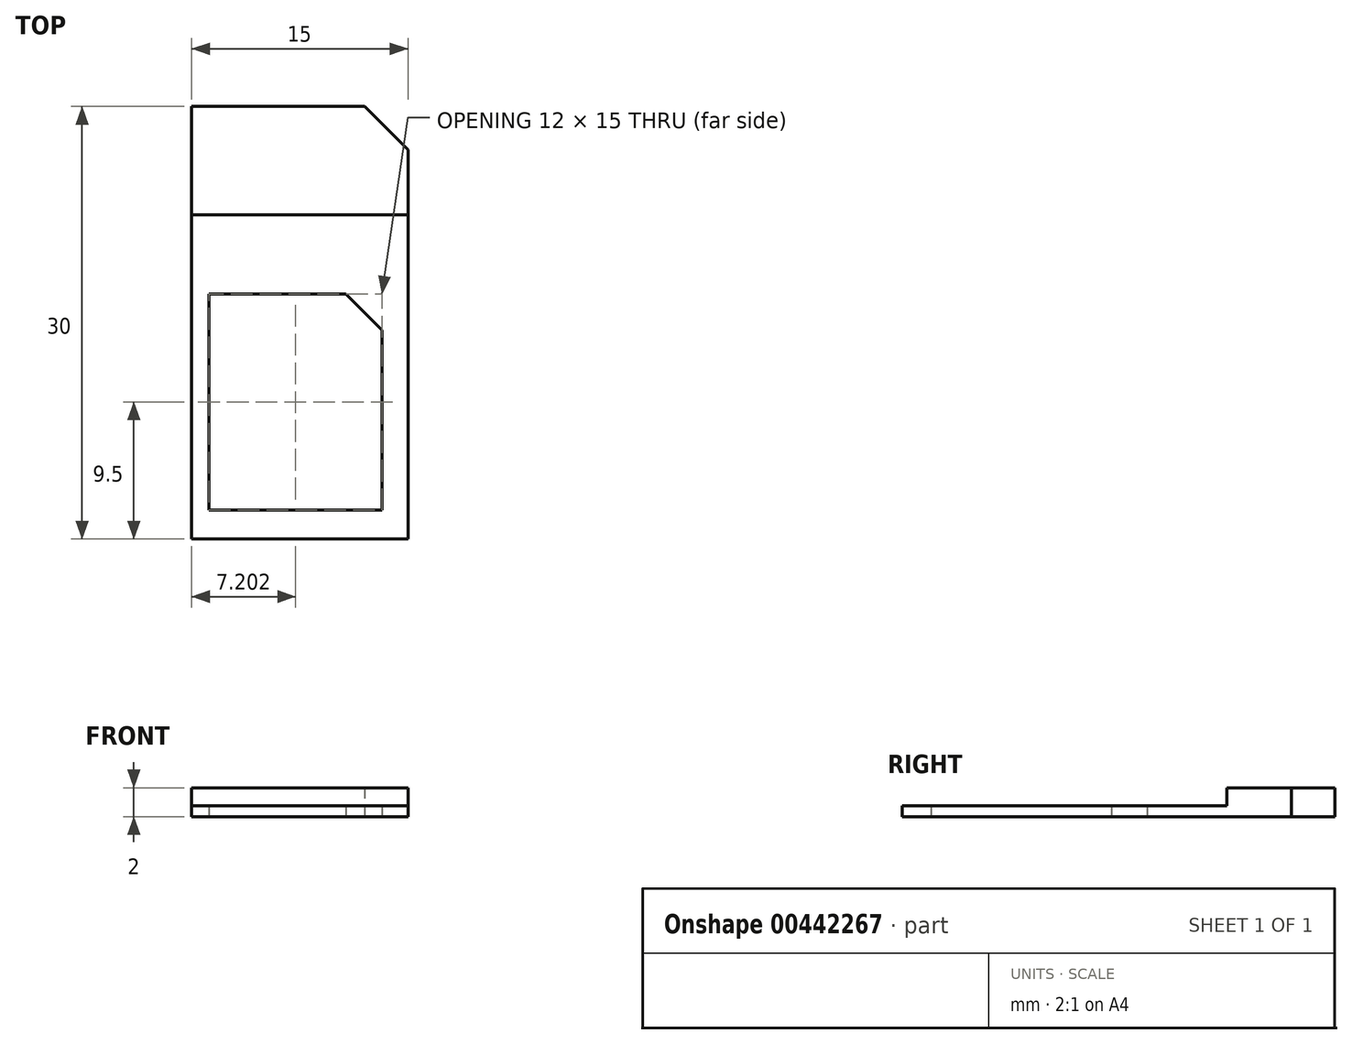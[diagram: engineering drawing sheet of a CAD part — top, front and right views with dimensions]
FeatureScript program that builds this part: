
annotation { "Feature Type Name" : "Feature", "Feature Type Description" : "" }
export const myFeature = defineFeature(function(context is Context, id is Id, definition is map)
    precondition{}
    {
        {
            var Q0;
            Q0=qCreatedBy(makeId("Top.planeOp"),FACE);
            var sketch = newSketch(context, id + "F0", { "sketchPlane" : qUnion([Q0])});
            skLineSegment(sketch, "E0.bottom", {"start": v(-32.09, -27) * mm, "end": v(-17.09, -27) * mm});
            skLineSegment(sketch, "E0.top", {"start": v(-32.09, 3) * mm, "end": v(-20.09, 3) * mm});
            skLineSegment(sketch, "E0.left", {"start": v(-32.09, -27) * mm, "end": v(-32.09, 3) * mm});
            skLineSegment(sketch, "E0.right", {"start": v(-17.09, -27) * mm, "end": v(-17.09, 0) * mm});
            skLineSegment(sketch, "E1", {"start": v(-20.09, 3) * mm, "end": v(-17.09, 0) * mm});
            skLineSegment(sketch, "E2.bottom", {"start": v(-30.89, -25) * mm, "end": v(-18.89, -25) * mm});
            skLineSegment(sketch, "E2.top", {"start": v(-30.89, -10) * mm, "end": v(-21.39, -10) * mm});
            skLineSegment(sketch, "E2.left", {"start": v(-30.89, -25) * mm, "end": v(-30.89, -10) * mm});
            skLineSegment(sketch, "E2.right", {"start": v(-18.89, -25) * mm, "end": v(-18.89, -12.5) * mm});
            skLineSegment(sketch, "E3", {"start": v(-21.39, -10) * mm, "end": v(-18.89, -12.5) * mm});
            skLineSegment(sketch, "E4", {"start": v(-32.09, -4.5) * mm, "end": v(-17.09, -4.5) * mm});
            skSolve(sketch);
        }
        {
            var Q0;
            Q0=makeQuery(id+"F0.imprint","IMPRINT",FACE,{"disambiguationData":[TD([[makeQuery(id+"F0.imprint","IMPRINT",EDGE,{"derivedFrom":sQuery(id+"F0.wireOp",EDGE,"E0.bottom")}),1.0]])]});
            extrude(context, id + "F1", {"entities" : qUnion([Q0]), "depth" : 0.75 * mm});
        }
        {
            var Q0;
            {var subQ4=sQuery(id+"F0.wireOp",EDGE,"E0.top");Q0=makeQuery(id+"F0.imprint","IMPRINT",FACE,{"disambiguationData":[TD([[makeQuery(id+"F0.imprint","IMPRINT",EDGE,{"derivedFrom":subQ4}),-1.0]])]});}
            extrude(context, id + "F2", {"entities" : qUnion([Q0]), "operationType" : NewBodyOperationType.ADD, "depth" : 2 * mm});
        }
    });
